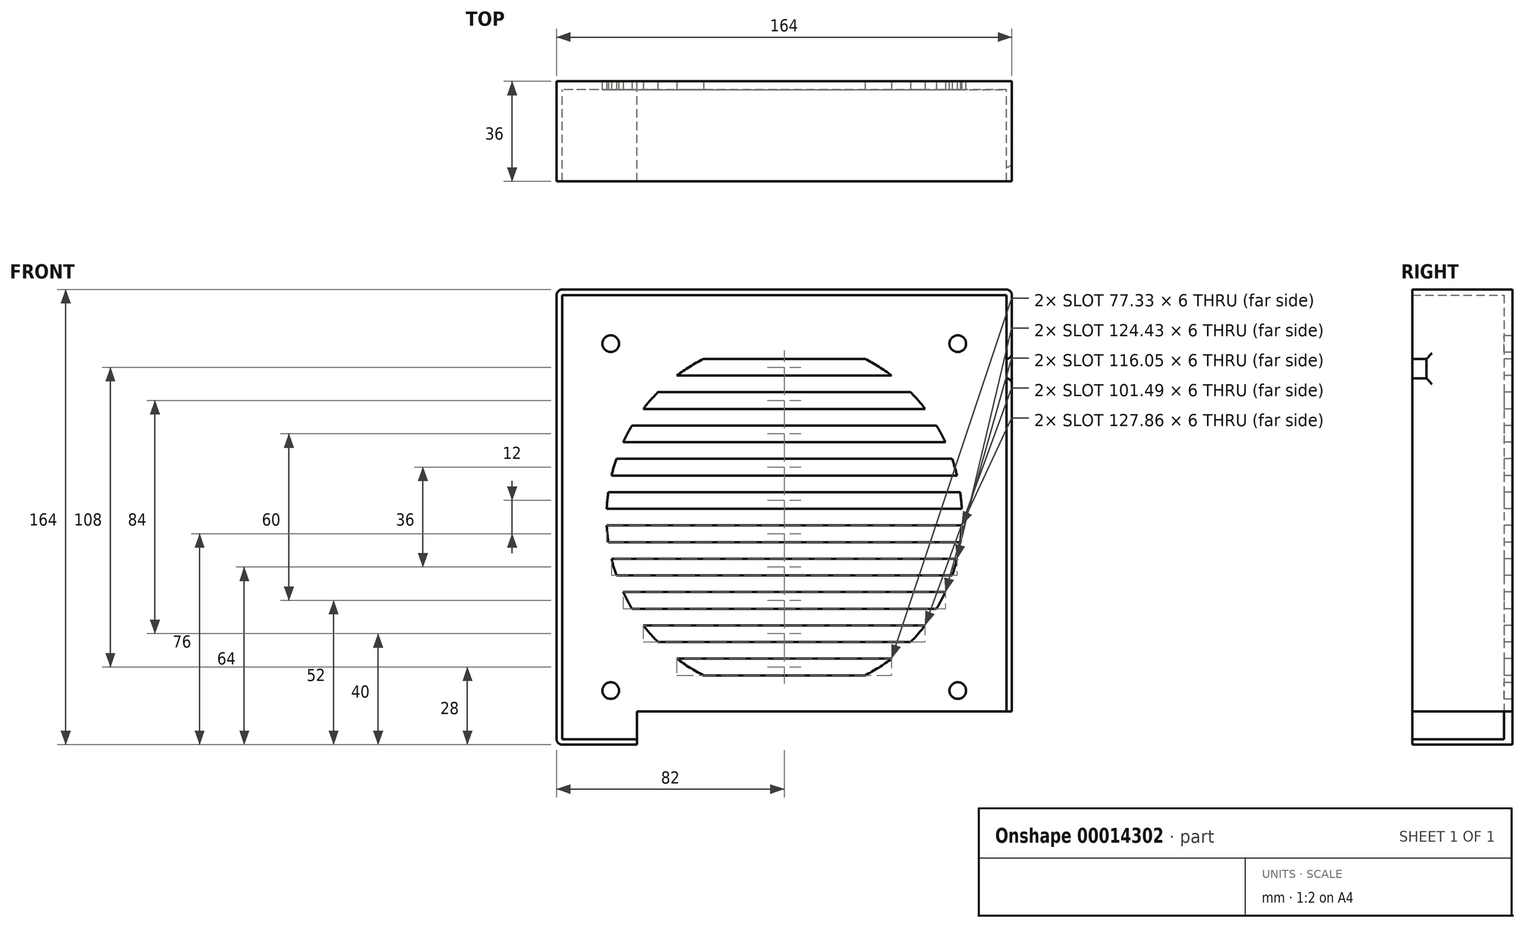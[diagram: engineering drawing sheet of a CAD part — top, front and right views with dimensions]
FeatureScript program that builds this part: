
annotation { "Feature Type Name" : "Feature", "Feature Type Description" : "" }
export const myFeature = defineFeature(function(context is Context, id is Id, definition is map)
    precondition{}
    {
        {
            var Q0;
            Q0=qCreatedBy(makeId("Front.planeOp"),FACE);
            var sketch = newSketch(context, id + "F0", { "sketchPlane" : qUnion([Q0])});
            skLineSegment(sketch, "E0.rect.bottom", {"start": v(-82, 82) * mm, "end": v(82, 82) * mm});
            skLineSegment(sketch, "E0.rect.left", {"start": v(-82, 82) * mm, "end": v(-82, -82) * mm});
            skPoint(sketch, "E0.rect.middle", {"position": v(0, 0) * mm});
            skCircle(sketch, "E1", {"center": v(-62.5, 62.5) * mm, "radius": 3 * mm});
            skCircle(sketch, "E2", {"center": v(62.5, 62.5) * mm, "radius": 3 * mm});
            skCircle(sketch, "E3", {"center": v(62.5, -62.5) * mm, "radius": 3 * mm});
            skCircle(sketch, "E4", {"center": v(-62.5, -62.5) * mm, "radius": 3 * mm});
            skLineSegment(sketch, "E5", {"start": v(-62.5, 62.5) * mm, "end": v(62.5, 62.5) * mm, "construction": true});
            skLineSegment(sketch, "E6", {"start": v(62.5, 62.5) * mm, "end": v(62.5, -62.5) * mm, "construction": true});
            skLineSegment(sketch, "E7", {"start": v(-62.5, -62.5) * mm, "end": v(62.5, -62.5) * mm, "construction": true});
            skLineSegment(sketch, "E8", {"start": v(-62.5, -62.5) * mm, "end": v(-62.5, 62.5) * mm, "construction": true});
            skLineSegment(sketch, "E9", {"start": v(-62.5, -62.5) * mm, "end": v(-62.5, -82) * mm, "construction": true});
            skLineSegment(sketch, "E10", {"start": v(-62.5, -62.5) * mm, "end": v(-82, -62.5) * mm, "construction": true});
            skLineSegment(sketch, "E11", {"start": v(62.5, 62.5) * mm, "end": v(62.5, 82) * mm, "construction": true});
            skLineSegment(sketch, "E12", {"start": v(62.5, 62.5) * mm, "end": v(82, 62.5) * mm, "construction": true});
            skLineSegment(sketch, "E13", {"start": v(0, 0) * mm, "end": v(0, -70) * mm, "construction": true});
            skLineSegment(sketch, "E14", {"start": v(-82, -70) * mm, "end": v(-53, -70) * mm, "construction": true});
            skLineSegment(sketch, "E15", {"start": v(-53, -70) * mm, "end": v(82, -70) * mm});
            skLineSegment(sketch, "E16", {"start": v(-53, -70) * mm, "end": v(-53, -82) * mm});
            skLineSegment(sketch, "E17", {"start": v(-53, -82) * mm, "end": v(-82, -82) * mm});
            skLineSegment(sketch, "E18", {"start": v(82, -70) * mm, "end": v(82, 82) * mm});
            skSolve(sketch);
        }
        {
            var Q0;
            Q0=qSketchRegion(id+"F0",true);
            extrude(context, id + "F1", {"entities" : qUnion([Q0]), "depth" : 3 * mm});
        }
        {
            var Q0;
            Q0=makeQuery(id+"F1.opExtrude","CAP_FACE",FACE,{"disambiguationData":[OSD([sQuery(id+"F0.wireOp",EDGE,"E0.rect.bottom"),sQuery(id+"F0.wireOp",EDGE,"E0.rect.top"),sQuery(id+"F0.wireOp",EDGE,"E0.rect.left"),sQuery(id+"F0.wireOp",EDGE,"E0.rect.right")])],"isStart":false});
            var sketch = newSketch(context, id + "F2", { "sketchPlane" : qUnion([Q0])});
            skLineSegment(sketch, "E19.rect.bottom", {"start": v(80, 80) * mm, "end": v(-80, 80) * mm});
            skLineSegment(sketch, "E19.rect.top", {"start": v(80, -80) * mm, "end": v(-80, -80) * mm});
            skLineSegment(sketch, "E19.rect.left", {"start": v(80, 80) * mm, "end": v(80, -80) * mm});
            skLineSegment(sketch, "E19.rect.right", {"start": v(-80, 80) * mm, "end": v(-80, -80) * mm});
            skPoint(sketch, "E19.rect.middle", {"position": v(0, 0) * mm});
            skLineSegment(sketch, "E20.rect.bottom", {"start": v(-82, 82) * mm, "end": v(82, 82) * mm});
            skLineSegment(sketch, "E20.rect.top", {"start": v(-82, -82) * mm, "end": v(82, -82) * mm});
            skLineSegment(sketch, "E20.rect.left", {"start": v(-82, 82) * mm, "end": v(-82, -82) * mm});
            skLineSegment(sketch, "E20.rect.right", {"start": v(82, 82) * mm, "end": v(82, -82) * mm});
            skLineSegment(sketch, "E21", {"start": v(-80, 80) * mm, "end": v(-80, 82) * mm, "construction": true});
            skLineSegment(sketch, "E22", {"start": v(-80, 73.83) * mm, "end": v(-82, 73.83) * mm, "construction": true});
            skLineSegment(sketch, "E23", {"start": v(-80, 67.42) * mm, "end": v(80, 67.42) * mm, "construction": true});
            skSolve(sketch);
        }
        {
            var Q0;
            Q0=makeQuery(id+"F2.imprint","IMPRINT",FACE,{"disambiguationData":[TD([[makeQuery(id+"F2.imprint","IMPRINT",EDGE,{"derivedFrom":sQuery(id+"F2.wireOp",EDGE,"E19.rect.bottom")}),-1.0]])]});
            extrude(context, id + "F3", {"entities" : qUnion([Q0]), "operationType" : NewBodyOperationType.ADD, "depth" : 28 * mm});
        }
        {
            var Q0;
            Q0=makeQuery(id+"F1.opExtrude","CAP_FACE",FACE,{"disambiguationData":[OSD([sQuery(id+"F0.wireOp",EDGE,"E0.rect.bottom"),sQuery(id+"F0.wireOp",EDGE,"E0.rect.top"),sQuery(id+"F0.wireOp",EDGE,"E0.rect.left"),sQuery(id+"F0.wireOp",EDGE,"E0.rect.right")])],"isStart":false});
            var sketch = newSketch(context, id + "F4", { "sketchPlane" : qUnion([Q0])});
            skCircle(sketch, "E24", {"center": v(0, 0) * mm, "radius": 64 * mm});
            skLineSegment(sketch, "E25", {"start": v(-63.93, 3) * mm, "end": v(63.93, 3) * mm});
            skLineSegment(sketch, "E26", {"start": v(-63.93, -3) * mm, "end": v(63.93, -3) * mm});
            skLineSegment(sketch, "E27", {"start": v(-63.36, 9) * mm, "end": v(63.36, 9) * mm});
            skLineSegment(sketch, "E28", {"start": v(-62.22, 15) * mm, "end": v(62.22, 15) * mm});
            skLineSegment(sketch, "E29", {"start": v(-63.36, -9) * mm, "end": v(63.36, -9) * mm});
            skLineSegment(sketch, "E30", {"start": v(-60.46, 21) * mm, "end": v(60.46, 21) * mm});
            skLineSegment(sketch, "E31", {"start": v(-58.03, 27) * mm, "end": v(58.03, 27) * mm});
            skLineSegment(sketch, "E32", {"start": v(-50.74, 39) * mm, "end": v(50.74, 39) * mm});
            skLineSegment(sketch, "E33", {"start": v(-45.5, 45) * mm, "end": v(45.5, 45) * mm});
            skLineSegment(sketch, "E34", {"start": v(-38.67, 51) * mm, "end": v(38.67, 51) * mm});
            skLineSegment(sketch, "E35", {"start": v(-29.1, 57) * mm, "end": v(29.1, 57) * mm});
            skLineSegment(sketch, "E36", {"start": v(-62.22, -15) * mm, "end": v(62.22, -15) * mm});
            skLineSegment(sketch, "E37", {"start": v(-60.46, -21) * mm, "end": v(60.46, -21) * mm});
            skLineSegment(sketch, "E38", {"start": v(-58.03, -27) * mm, "end": v(58.03, -27) * mm});
            skLineSegment(sketch, "E39", {"start": v(-54.84, -33) * mm, "end": v(54.84, -33) * mm});
            skLineSegment(sketch, "E40", {"start": v(-50.74, -39) * mm, "end": v(50.74, -39) * mm});
            skLineSegment(sketch, "E41", {"start": v(-45.5, -45) * mm, "end": v(45.5, -45) * mm});
            skLineSegment(sketch, "E42", {"start": v(-38.67, -51) * mm, "end": v(38.67, -51) * mm});
            skLineSegment(sketch, "E43", {"start": v(-29.1, -57) * mm, "end": v(29.1, -57) * mm});
            skLineSegment(sketch, "E44", {"start": v(-54.84, 33) * mm, "end": v(54.84, 33) * mm});
            skSolve(sketch);
        }
        {
            var Q0;
            {var subQ1=sQuery(id+"F4.wireOp",EDGE,"E25");Q0=makeQuery(id+"F4.imprint","IMPRINT",FACE,{"disambiguationData":[TD([[makeQuery(id+"F4.imprint","IMPRINT",EDGE,{"derivedFrom":subQ1}),1.0]])]});}
            var Q1;
            {var subQ1=sQuery(id+"F4.wireOp",EDGE,"E26");Q1=makeQuery(id+"F4.imprint","IMPRINT",FACE,{"disambiguationData":[TD([[makeQuery(id+"F4.imprint","IMPRINT",EDGE,{"derivedFrom":subQ1}),-1.0]])]});}
            var Q2;
            {var subQ0=sQuery(id+"F4.wireOp",EDGE,"E28");Q2=makeQuery(id+"F4.imprint","IMPRINT",FACE,{"disambiguationData":[TD([[makeQuery(id+"F4.imprint","IMPRINT",EDGE,{"derivedFrom":subQ0}),1.0]])]});}
            var Q3;
            {var subQ1=sQuery(id+"F4.wireOp",EDGE,"E36");Q3=makeQuery(id+"F4.imprint","IMPRINT",FACE,{"disambiguationData":[TD([[makeQuery(id+"F4.imprint","IMPRINT",EDGE,{"derivedFrom":subQ1}),-1.0]])]});}
            var Q4;
            {var subQ1=sQuery(id+"F4.wireOp",EDGE,"E38");Q4=makeQuery(id+"F4.imprint","IMPRINT",FACE,{"disambiguationData":[TD([[makeQuery(id+"F4.imprint","IMPRINT",EDGE,{"derivedFrom":subQ1}),-1.0]])]});}
            var Q5;
            {var subQ1=sQuery(id+"F4.wireOp",EDGE,"E40");Q5=makeQuery(id+"F4.imprint","IMPRINT",FACE,{"disambiguationData":[TD([[makeQuery(id+"F4.imprint","IMPRINT",EDGE,{"derivedFrom":subQ1}),-1.0]])]});}
            var Q6;
            {var subQ1=sQuery(id+"F4.wireOp",EDGE,"E42");Q6=makeQuery(id+"F4.imprint","IMPRINT",FACE,{"disambiguationData":[TD([[makeQuery(id+"F4.imprint","IMPRINT",EDGE,{"derivedFrom":subQ1}),-1.0]])]});}
            var Q7;
            {var subQ1=sQuery(id+"F4.wireOp",EDGE,"E31");Q7=makeQuery(id+"F4.imprint","IMPRINT",FACE,{"disambiguationData":[TD([[makeQuery(id+"F4.imprint","IMPRINT",EDGE,{"derivedFrom":subQ1}),1.0]])]});}
            var Q8;
            {var subQ1=sQuery(id+"F4.wireOp",EDGE,"E32");Q8=makeQuery(id+"F4.imprint","IMPRINT",FACE,{"disambiguationData":[TD([[makeQuery(id+"F4.imprint","IMPRINT",EDGE,{"derivedFrom":subQ1}),1.0]])]});}
            var Q9;
            {var subQ1=sQuery(id+"F4.wireOp",EDGE,"E34");Q9=makeQuery(id+"F4.imprint","IMPRINT",FACE,{"disambiguationData":[TD([[makeQuery(id+"F4.imprint","IMPRINT",EDGE,{"derivedFrom":subQ1}),1.0]])]});}
            extrude(context, id + "F5", {"entities" : qUnion([Q0, Q1, Q2, Q3, Q4, Q5, Q6, Q7, Q8, Q9]), "operationType" : NewBodyOperationType.REMOVE, "oppositeDirection" : true, "depth" : 3 * mm});
        }
        {
            var Q0;
            Q0=makeQuery(id+"F3.opExtrude","CAP_FACE",FACE,{"disambiguationData":[OSD([sQuery(id+"F0.wireOp",EDGE,"E15"),sQuery(id+"F0.wireOp",EDGE,"E16"),sQuery(id+"F2.wireOp",EDGE,"E19.rect.bottom"),sQuery(id+"F2.wireOp",EDGE,"E19.rect.top"),sQuery(id+"F2.wireOp",EDGE,"E19.rect.left"),sQuery(id+"F2.wireOp",EDGE,"E19.rect.right"),sQuery(id+"F2.wireOp",EDGE,"E20.rect.bottom"),sQuery(id+"F2.wireOp",EDGE,"E20.rect.top"),sQuery(id+"F2.wireOp",EDGE,"E20.rect.left"),sQuery(id+"F2.wireOp",EDGE,"E20.rect.right")])],"isStart":false});
            var sketch = newSketch(context, id + "F6", { "sketchPlane" : qUnion([Q0])});
            skLineSegment(sketch, "E45", {"start": v(-80, -80) * mm, "end": v(-80, 80) * mm});
            skLineSegment(sketch, "E46", {"start": v(-80, 80) * mm, "end": v(80, 80) * mm});
            skLineSegment(sketch, "E47", {"start": v(80, 80) * mm, "end": v(80, 57) * mm});
            skLineSegment(sketch, "E48", {"start": v(-82, 82) * mm, "end": v(-82, -82) * mm});
            skLineSegment(sketch, "E49", {"start": v(-82, 82) * mm, "end": v(82, 82) * mm});
            skLineSegment(sketch, "E50", {"start": v(-82, -82) * mm, "end": v(-53, -82) * mm});
            skLineSegment(sketch, "E51", {"start": v(82, -70) * mm, "end": v(82, 50) * mm});
            skLineSegment(sketch, "E52", {"start": v(82, 57) * mm, "end": v(82, 82) * mm});
            skLineSegment(sketch, "E53", {"start": v(-80, -80) * mm, "end": v(-53, -80) * mm});
            skLineSegment(sketch, "E54", {"start": v(-53, -80) * mm, "end": v(-53, -82) * mm});
            skLineSegment(sketch, "E55", {"start": v(82, -70) * mm, "end": v(80, -70) * mm});
            skLineSegment(sketch, "E56", {"start": v(80, -70) * mm, "end": v(80, 50) * mm});
            skLineSegment(sketch, "E57", {"start": v(80, 50) * mm, "end": v(82, 50) * mm});
            skLineSegment(sketch, "E58", {"start": v(80, 57) * mm, "end": v(82, 57) * mm});
            skSolve(sketch);
        }
        {
            var Q0;
            Q0 = qSketchRegion(id + "F6", true);
            extrude(context, id + "F7", {"entities" : qUnion([Q0]), "operationType" : NewBodyOperationType.ADD, "depth" : 5 * mm});
        }
        {
            var Q0;
            Q0=makeQuery(id+"F7.boolean.opBoolean","MERGE",EDGE,{"derivedFrom":[makeQuery(id+"F3.boolean.opBoolean","MERGE",EDGE,{"derivedFrom":[makeQuery(id+"F1.opExtrude","SWEPT_EDGE",EDGE,{"disambiguationData":[OSD([sQuery(id+"F0.wireOp",EDGE,"E0.rect.bottom"),sQuery(id+"F0.wireOp",EDGE,"E0.rect.left")])]}),makeQuery(id+"F3.opExtrude","SWEPT_EDGE",EDGE,{"disambiguationData":[OSD([sQuery(id+"F2.wireOp",EDGE,"E20.rect.bottom"),sQuery(id+"F2.wireOp",EDGE,"E20.rect.left")])]})]}),makeQuery(id+"F7.opExtrude","SWEPT_EDGE",EDGE,{"disambiguationData":[OSD([sQuery(id+"F6.wireOp",EDGE,"E48"),sQuery(id+"F6.wireOp",EDGE,"E49")])]})]});
            var Q1;
            Q1=makeQuery(id+"F7.boolean.opBoolean","MERGE",EDGE,{"derivedFrom":[makeQuery(id+"F3.boolean.opBoolean","MERGE",EDGE,{"derivedFrom":[makeQuery(id+"F1.opExtrude","SWEPT_EDGE",EDGE,{"disambiguationData":[OSD([sQuery(id+"F0.wireOp",EDGE,"E0.rect.left"),sQuery(id+"F0.wireOp",EDGE,"E17")])]}),makeQuery(id+"F3.opExtrude","SWEPT_EDGE",EDGE,{"disambiguationData":[OSD([sQuery(id+"F2.wireOp",EDGE,"E20.rect.top"),sQuery(id+"F2.wireOp",EDGE,"E20.rect.left")])]})]}),makeQuery(id+"F7.opExtrude","SWEPT_EDGE",EDGE,{"disambiguationData":[OSD([sQuery(id+"F6.wireOp",EDGE,"E48"),sQuery(id+"F6.wireOp",EDGE,"E50")])]})]});
            var Q2;
            Q2=makeQuery(id+"F7.boolean.opBoolean","MERGE",EDGE,{"derivedFrom":[makeQuery(id+"F3.boolean.opBoolean","MERGE",EDGE,{"derivedFrom":[makeQuery(id+"F1.opExtrude","SWEPT_EDGE",EDGE,{"disambiguationData":[OSD([sQuery(id+"F0.wireOp",EDGE,"E0.rect.bottom"),sQuery(id+"F0.wireOp",EDGE,"E18")])]}),makeQuery(id+"F3.opExtrude","SWEPT_EDGE",EDGE,{"disambiguationData":[OSD([sQuery(id+"F2.wireOp",EDGE,"E20.rect.bottom"),sQuery(id+"F2.wireOp",EDGE,"E20.rect.right")])]})]}),makeQuery(id+"F7.opExtrude","SWEPT_EDGE",EDGE,{"disambiguationData":[OSD([sQuery(id+"F6.wireOp",EDGE,"E49"),sQuery(id+"F6.wireOp",EDGE,"E52")])]})]});
            var Q3;
            Q3=makeQuery(id+"F3.opExtrude","CAP_EDGE",EDGE,{"disambiguationData":[OSD([sQuery(id+"F2.wireOp",EDGE,"E20.rect.right")])],"isStart":false});
            var Q4;
            Q4=makeQuery(id+"F7.opExtrude","SWEPT_EDGE",EDGE,{"disambiguationData":[OSD([sQuery(id+"F2.wireOp",EDGE,"E20.rect.right"),sQuery(id+"F6.wireOp",EDGE,"E52"),sQuery(id+"F6.wireOp",EDGE,"E58")])]});
            var Q5;
            Q5=makeQuery(id+"F7.opExtrude","SWEPT_EDGE",EDGE,{"disambiguationData":[OSD([sQuery(id+"F2.wireOp",EDGE,"E20.rect.right"),sQuery(id+"F6.wireOp",EDGE,"E51"),sQuery(id+"F6.wireOp",EDGE,"E57")])]});
            fillet(context, id + "F8", {"entities" : qUnion([Q0, Q1, Q2, Q3, Q4, Q5]), "radius" : 2 * mm, "tangentPropagation" : true, "allowEdgeOverflow" : false});
        }
    });
